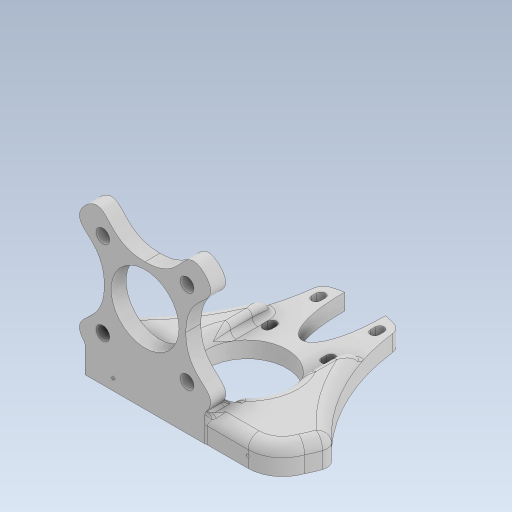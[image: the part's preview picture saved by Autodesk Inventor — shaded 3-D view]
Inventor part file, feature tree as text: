
AUTODESK INVENTOR PART (.ipt)
format: ipt  version: 2023 (Build 270158000, 158)  size: 1,891,840 bytes
history: native  units: in
note: dims shown in document units (in); Inventor stores cm internally (conversion verified against a paired STEP export)
features: sketch x7, extrude x6, fillet x4, plane x4, projected_geometry x4
ambient origin geometry x8: Origin, YZ Plane, XZ Plane, XY Plane, X Axis, Y Axis, Z Axis, Center Point
bodies: Solid1 (feature_tree)
feature tree (25):
  extrude  "Extrusion1"  Depth=0.3937in
  fillet  "Fillet2"  Radius=5.9055in
  plane  "Work Plane1"
  extrude  "Extrusion3"  Depth=0.5906in
  fillet  "Fillet3"  Radius=3.0187in
  extrude  "Extrusion4"  Depth=0.0098in
  plane  "Work Plane2"
  sketch  "Sketch7"  dims[d23=0.0394in d24=0.0394in d25=0.5592in d26=0.5592in]
  plane  "Work Plane4"
  extrude  "Extrusion9"  Depth=0.0787in TaperAngle=0.0deg
  extrude  "Extrusion12"  Depth=0.0394in
  fillet  "Fillet8"  Radius=0.5592in
  fillet  "Fillet9"  Radius=0.5592in
  extrude  "Extrusion5"  Depth=0.7067in TaperAngle=0.0deg
  sketch  "Sketch1"  dims[d5=0.3937in d6=0.0in d9=1.0in d13=5.9055in]
  sketch  "Sketch3"  dims[d14=0.1575in d15=0.5906in d16=3.0187in d17=0.0in]
  sketch  "Sketch4"  dims[d18=0.0787in d19=0.0098in]
  projected_geometry  "Projected Loop1"
  projected_geometry  "Projected Loop2"
  sketch  "Sketch5"  dims[d20=0.0098in d21=0.0787in d22=0.0in]
  projected_geometry  "Projected Loop3"
  plane  "Work Plane3"
  sketch  "Sketch9"  dims[d27=0.1575in d28=0.7067in d29=0.0in]
  sketch  "Sketch13"  dims[d32=1.7323in d33=1.5748in d34=0.1969in d35=0.7087in d36=0.5118in d46=90.0deg d47=1.1811in d48=1.5748in d49=1.2205in d50=1.2205in d51=0.1969in d52=1.5748in d54=360.0deg d56=0.9843in d57=1.7323in d60=0.2165in d61=0.0in d68=0.3937in d69=0.0787in d70=0.0in d71=0.0787in d72=0.0787in d73=0.7009in d74=0.1969in d75=0.1575in d76=0.315in d58=0.0197in d59=0.0344in]
  projected_geometry  "Projected Loop10"
